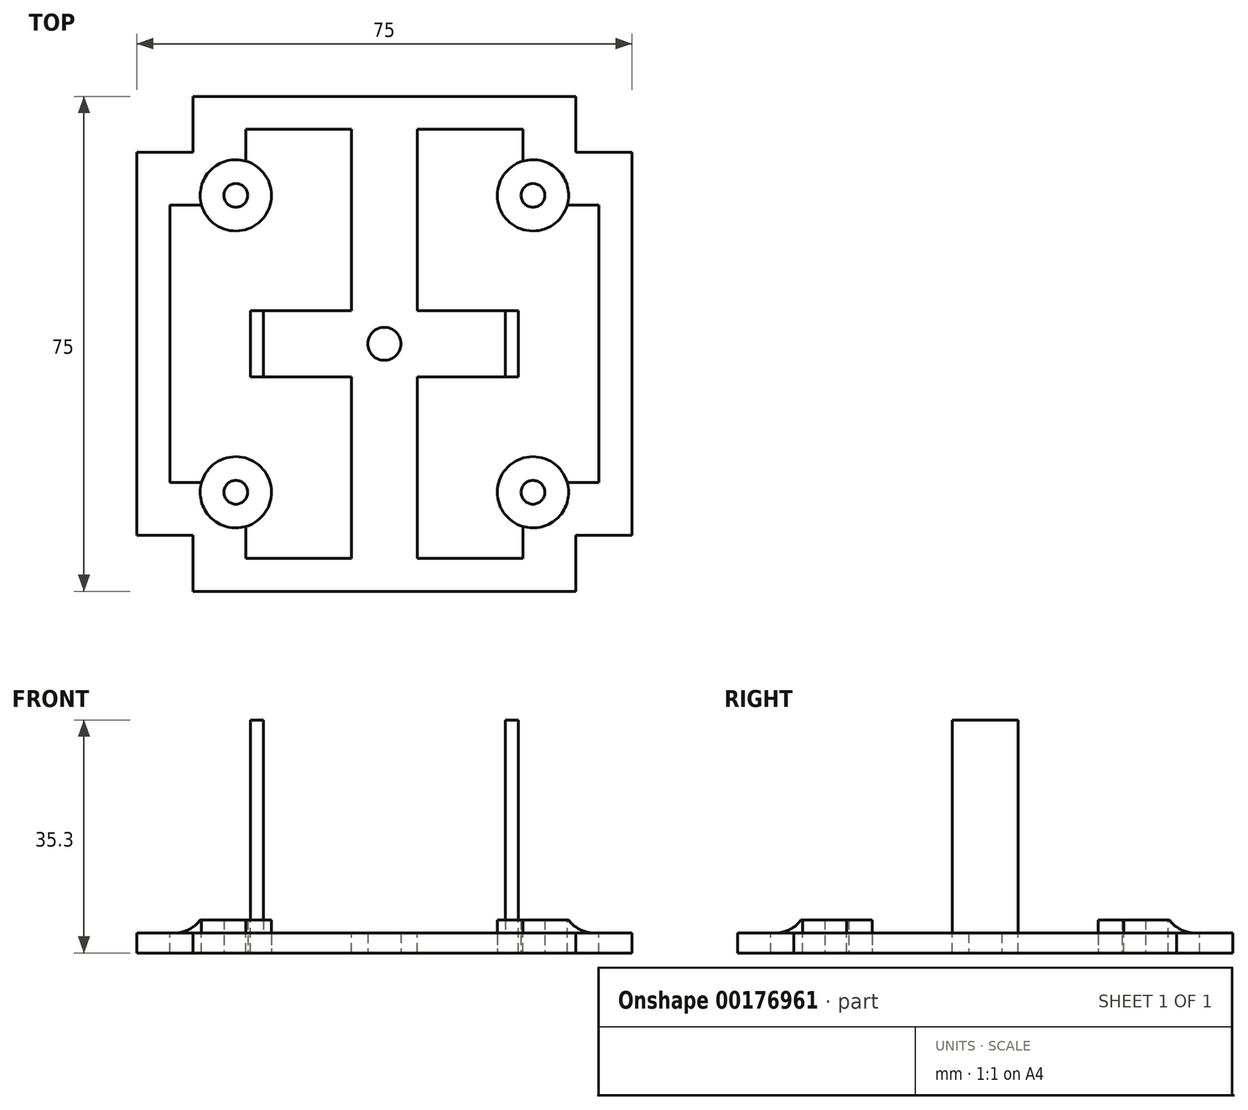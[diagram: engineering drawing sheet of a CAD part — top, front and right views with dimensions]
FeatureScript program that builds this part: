
annotation { "Feature Type Name" : "Feature", "Feature Type Description" : "" }
export const myFeature = defineFeature(function(context is Context, id is Id, definition is map)
    precondition{}
    {
        {
            assignVariable(context, id + "F0", {"name" : "thickness", "anyValue" : 3});
        }
        {
            var Q0;
            Q0=qCreatedBy(makeId("Top.planeOp"),FACE);
            var sketch = newSketch(context, id + "F1", { "sketchPlane" : qUnion([Q0])});
            skLineSegment(sketch, "E0.bottom", {"start": v(29, 37.5) * mm, "end": v(-29, 37.5) * mm});
            skLineSegment(sketch, "E0.top", {"start": v(29, -37.5) * mm, "end": v(-29, -37.5) * mm});
            skLineSegment(sketch, "E0.right", {"start": v(-37.5, 29) * mm, "end": v(-37.5, -29) * mm});
            skPoint(sketch, "E0.middle", {"position": v(0, 0) * mm});
            skLineSegment(sketch, "E1", {"start": v(-37.5, 29) * mm, "end": v(-29, 29) * mm});
            skLineSegment(sketch, "E2", {"start": v(-29, 29) * mm, "end": v(-29, 37.5) * mm});
            skLineSegment(sketch, "E3", {"start": v(0, 0) * mm, "end": v(0, 37.5) * mm, "construction": true});
            skLineSegment(sketch, "E4", {"start": v(0, 0) * mm, "end": v(50, 0) * mm, "construction": true});
            skLineSegment(sketch, "E5.MirrorCS", {"start": v(29, 29) * mm, "end": v(29, 37.5) * mm});
            skLineSegment(sketch, "E6.MirrorCS", {"start": v(37.5, 29) * mm, "end": v(29, 29) * mm});
            skLineSegment(sketch, "E7.MirrorCS", {"start": v(-37.5, -29) * mm, "end": v(-29, -29) * mm});
            skLineSegment(sketch, "E8.MirrorCS", {"start": v(-29, -29) * mm, "end": v(-29, -37.5) * mm});
            skLineSegment(sketch, "E9.MirrorCS", {"start": v(37.5, -29) * mm, "end": v(29, -29) * mm});
            skLineSegment(sketch, "E10.MirrorCS", {"start": v(37.5, -29) * mm, "end": v(37.5, 29) * mm});
            skLineSegment(sketch, "E11.MirrorCS", {"start": v(29, -29) * mm, "end": v(29, -37.5) * mm});
            skCircle(sketch, "E12", {"center": v(0, 0) * mm, "radius": 2.5 * mm});
            skSolve(sketch);
        }
        {
            var Q0;
            Q0=makeQuery(id+"F1.imprint","IMPRINT",FACE,{"disambiguationData":[TD([[makeQuery(id+"F1.imprint","IMPRINT",EDGE,{"derivedFrom":sQuery(id+"F1.wireOp",EDGE,"E0.bottom")}),1.0]])]});
            extrude(context, id + "F2", {"entities" : qUnion([Q0]), "depth" : (getVariable(context, 'thickness')) * mm});
        }
        {
            var Q0;
            Q0=makeQuery(id+"F2.opExtrude","CAP_FACE",FACE,{"disambiguationData":[OSD([sQuery(id+"F1.wireOp",EDGE,"E0.bottom"),sQuery(id+"F1.wireOp",EDGE,"E0.right"),sQuery(id+"F1.wireOp",EDGE,"E1"),sQuery(id+"F1.wireOp",EDGE,"E2"),sQuery(id+"F1.wireOp",EDGE,"E5.MirrorCS"),sQuery(id+"F1.wireOp",EDGE,"E6.MirrorCS"),sQuery(id+"F1.wireOp",EDGE,"E7.MirrorCS"),sQuery(id+"F1.wireOp",EDGE,"E8.MirrorCS"),sQuery(id+"F1.wireOp",EDGE,"E9.MirrorCS"),sQuery(id+"F1.wireOp",EDGE,"E10.MirrorCS"),sQuery(id+"F1.wireOp",EDGE,"E11.MirrorCS"),sQuery(id+"F1.wireOp",EDGE,"E0.top"),sQuery(id+"F1.wireOp",EDGE,"E12")])],"isStart":false});
            var sketch = newSketch(context, id + "F3", { "sketchPlane" : qUnion([Q0])});
            skPoint(sketch, "E13.middle", {"position": v(0, 0) * mm});
            skLineSegment(sketch, "E14.0", {"start": v(5, -32.5) * mm, "end": v(5, -5) * mm});
            skLineSegment(sketch, "E15.0", {"start": v(-5, -32.5) * mm, "end": v(-5, -5) * mm});
            skLineSegment(sketch, "E16", {"start": v(-17.9, -22.5) * mm, "end": v(17.9, -22.5) * mm, "construction": true});
            skLineSegment(sketch, "E17", {"start": v(-17.9, -22.5) * mm, "end": v(-17.9, 37.5) * mm, "construction": true});
            skLineSegment(sketch, "E18", {"start": v(17.9, -22.5) * mm, "end": v(17.9, 37.5) * mm, "construction": true});
            skLineSegment(sketch, "E19", {"start": v(-20.3, 5) * mm, "end": v(-5, 5) * mm});
            skLineSegment(sketch, "E20.MirrorCS", {"start": v(-20.3, -5) * mm, "end": v(-5, -5) * mm});
            skLineSegment(sketch, "E21.trimOffspring", {"start": v(-20.3, -5) * mm, "end": v(-20.3, 5) * mm});
            skLineSegment(sketch, "E22.MirrorCS", {"start": v(20.3, -5) * mm, "end": v(20.3, 5) * mm});
            skLineSegment(sketch, "E23.0", {"start": v(21, 32.5) * mm, "end": v(-21, 32.5) * mm});
            skLineSegment(sketch, "E24.0", {"start": v(-32.5, 21) * mm, "end": v(-32.5, -21) * mm});
            skLineSegment(sketch, "E25.0", {"start": v(-32.5, 21) * mm, "end": v(-21, 21) * mm});
            skLineSegment(sketch, "E26.0", {"start": v(-21, 21) * mm, "end": v(-21, 32.5) * mm});
            skLineSegment(sketch, "E27.MirrorCS", {"start": v(21, 21) * mm, "end": v(21, 32.5) * mm});
            skLineSegment(sketch, "E28.MirrorCS", {"start": v(32.5, 21) * mm, "end": v(21, 21) * mm});
            skLineSegment(sketch, "E29.MirrorCS", {"start": v(32.5, 21) * mm, "end": v(32.5, -21) * mm});
            skLineSegment(sketch, "E30.MirrorCS", {"start": v(32.5, -21) * mm, "end": v(21, -21) * mm});
            skLineSegment(sketch, "E31.MirrorCS", {"start": v(21, -21) * mm, "end": v(21, -32.5) * mm});
            skLineSegment(sketch, "E32.MirrorCS", {"start": v(21, -32.5) * mm, "end": v(-21, -32.5) * mm});
            skLineSegment(sketch, "E33.MirrorCS", {"start": v(-21, -21) * mm, "end": v(-21, -32.5) * mm});
            skLineSegment(sketch, "E34.MirrorCS", {"start": v(-32.5, -21) * mm, "end": v(-21, -21) * mm});
            skLineSegment(sketch, "E35.trimOffspring", {"start": v(-5, 5) * mm, "end": v(-5, 32.5) * mm});
            skLineSegment(sketch, "E36.trimOffspring", {"start": v(5, 5) * mm, "end": v(5, 32.5) * mm});
            skLineSegment(sketch, "E37.trimOffspring", {"start": v(5, 5) * mm, "end": v(20.3, 5) * mm});
            skLineSegment(sketch, "E38.trimOffspring", {"start": v(5, -5) * mm, "end": v(20.3, -5) * mm});
            skSolve(sketch);
        }
        {
            var Q0;
            {var subQ4=sQuery(id+"F3.wireOp",EDGE,"E15.0");Q0=makeQuery(id+"F3.imprint","IMPRINT",FACE,{"disambiguationData":[TD([[makeQuery(id+"F3.imprint","IMPRINT",EDGE,{"derivedFrom":subQ4}),1.0]])]});}
            var Q1;
            {var subQ5=sQuery(id+"F3.wireOp",EDGE,"E14.0");Q1=makeQuery(id+"F3.imprint","IMPRINT",FACE,{"disambiguationData":[TD([[makeQuery(id+"F3.imprint","IMPRINT",EDGE,{"derivedFrom":subQ5}),-1.0]])]});}
            extrude(context, id + "F4", {"entities" : qUnion([Q0, Q1]), "operationType" : NewBodyOperationType.REMOVE, "endBound" : BoundingType.THROUGH_ALL, "oppositeDirection" : true, "depth" : 25 * mm});
        }
        {
            var Q0;
            Q0=makeQuery(id+"F2.opExtrude","CAP_FACE",FACE,{"disambiguationData":[OSD([sQuery(id+"F1.wireOp",EDGE,"E0.bottom"),sQuery(id+"F1.wireOp",EDGE,"E0.right"),sQuery(id+"F1.wireOp",EDGE,"E1"),sQuery(id+"F1.wireOp",EDGE,"E2"),sQuery(id+"F1.wireOp",EDGE,"E5.MirrorCS"),sQuery(id+"F1.wireOp",EDGE,"E6.MirrorCS"),sQuery(id+"F1.wireOp",EDGE,"E7.MirrorCS"),sQuery(id+"F1.wireOp",EDGE,"E8.MirrorCS"),sQuery(id+"F1.wireOp",EDGE,"E9.MirrorCS"),sQuery(id+"F1.wireOp",EDGE,"E10.MirrorCS"),sQuery(id+"F1.wireOp",EDGE,"E11.MirrorCS"),sQuery(id+"F1.wireOp",EDGE,"E0.top"),sQuery(id+"F1.wireOp",EDGE,"E12")])],"isStart":false});
            var sketch = newSketch(context, id + "F5", { "sketchPlane" : qUnion([Q0])});
            skCircle(sketch, "E39", {"center": v(-22.5, 22.5) * mm, "radius": 1.8 * mm});
            skCircle(sketch, "E40", {"center": v(-22.5, 22.5) * mm, "radius": 5.4 * mm});
            skCircle(sketch, "E41.MirrorC", {"center": v(-22.5, -22.5) * mm, "radius": 1.8 * mm});
            skCircle(sketch, "E42.MirrorC", {"center": v(-22.5, -22.5) * mm, "radius": 5.4 * mm});
            skCircle(sketch, "E43.MirrorC", {"center": v(22.5, 22.5) * mm, "radius": 1.8 * mm});
            skCircle(sketch, "E44.MirrorC", {"center": v(22.5, 22.5) * mm, "radius": 5.4 * mm});
            skCircle(sketch, "E45.MirrorC", {"center": v(22.5, -22.5) * mm, "radius": 5.4 * mm});
            skCircle(sketch, "E46.MirrorC", {"center": v(22.5, -22.5) * mm, "radius": 1.8 * mm});
            skSolve(sketch);
        }
        {
            var Q0;
            Q0=qSketchRegion(id+"F5",true);
            extrude(context, id + "F6", {"entities" : qUnion([Q0]), "operationType" : NewBodyOperationType.ADD, "depth" : 2 * mm});
        }
        {
            var Q0;
            Q0=makeQuery(id+"F6.boolean.opBoolean","SPLIT",FACE,{"disambiguationData":[TD([makeQuery(id+"F6.opExtrude","SWEPT_FACE",FACE,{"disambiguationData":[OSD([sQuery(id+"F5.wireOp",EDGE,"E39")])]})])],"derivedFrom":makeQuery(id+"F2.opExtrude","CAP_FACE",FACE,{"disambiguationData":[OSD([sQuery(id+"F1.wireOp",EDGE,"E0.bottom"),sQuery(id+"F1.wireOp",EDGE,"E0.right"),sQuery(id+"F1.wireOp",EDGE,"E1"),sQuery(id+"F1.wireOp",EDGE,"E2"),sQuery(id+"F1.wireOp",EDGE,"E5.MirrorCS"),sQuery(id+"F1.wireOp",EDGE,"E6.MirrorCS"),sQuery(id+"F1.wireOp",EDGE,"E7.MirrorCS"),sQuery(id+"F1.wireOp",EDGE,"E8.MirrorCS"),sQuery(id+"F1.wireOp",EDGE,"E9.MirrorCS"),sQuery(id+"F1.wireOp",EDGE,"E10.MirrorCS"),sQuery(id+"F1.wireOp",EDGE,"E11.MirrorCS"),sQuery(id+"F1.wireOp",EDGE,"E0.top"),sQuery(id+"F1.wireOp",EDGE,"E12")])],"isStart":false})});
            var Q1;
            Q1=makeQuery(id+"F6.boolean.opBoolean","SPLIT",FACE,{"disambiguationData":[TD([makeQuery(id+"F6.opExtrude","SWEPT_FACE",FACE,{"disambiguationData":[OSD([sQuery(id+"F5.wireOp",EDGE,"E43.MirrorC")])]})])],"derivedFrom":makeQuery(id+"F2.opExtrude","CAP_FACE",FACE,{"disambiguationData":[OSD([sQuery(id+"F1.wireOp",EDGE,"E0.bottom"),sQuery(id+"F1.wireOp",EDGE,"E0.right"),sQuery(id+"F1.wireOp",EDGE,"E1"),sQuery(id+"F1.wireOp",EDGE,"E2"),sQuery(id+"F1.wireOp",EDGE,"E5.MirrorCS"),sQuery(id+"F1.wireOp",EDGE,"E6.MirrorCS"),sQuery(id+"F1.wireOp",EDGE,"E7.MirrorCS"),sQuery(id+"F1.wireOp",EDGE,"E8.MirrorCS"),sQuery(id+"F1.wireOp",EDGE,"E9.MirrorCS"),sQuery(id+"F1.wireOp",EDGE,"E10.MirrorCS"),sQuery(id+"F1.wireOp",EDGE,"E11.MirrorCS"),sQuery(id+"F1.wireOp",EDGE,"E0.top"),sQuery(id+"F1.wireOp",EDGE,"E12")])],"isStart":false})});
            var Q2;
            Q2=makeQuery(id+"F6.boolean.opBoolean","SPLIT",FACE,{"disambiguationData":[TD([makeQuery(id+"F6.opExtrude","SWEPT_FACE",FACE,{"disambiguationData":[OSD([sQuery(id+"F5.wireOp",EDGE,"E46.MirrorC")])]})])],"derivedFrom":makeQuery(id+"F2.opExtrude","CAP_FACE",FACE,{"disambiguationData":[OSD([sQuery(id+"F1.wireOp",EDGE,"E0.bottom"),sQuery(id+"F1.wireOp",EDGE,"E0.right"),sQuery(id+"F1.wireOp",EDGE,"E1"),sQuery(id+"F1.wireOp",EDGE,"E2"),sQuery(id+"F1.wireOp",EDGE,"E5.MirrorCS"),sQuery(id+"F1.wireOp",EDGE,"E6.MirrorCS"),sQuery(id+"F1.wireOp",EDGE,"E7.MirrorCS"),sQuery(id+"F1.wireOp",EDGE,"E8.MirrorCS"),sQuery(id+"F1.wireOp",EDGE,"E9.MirrorCS"),sQuery(id+"F1.wireOp",EDGE,"E10.MirrorCS"),sQuery(id+"F1.wireOp",EDGE,"E11.MirrorCS"),sQuery(id+"F1.wireOp",EDGE,"E0.top"),sQuery(id+"F1.wireOp",EDGE,"E12")])],"isStart":false})});
            var Q3;
            Q3=makeQuery(id+"F6.boolean.opBoolean","SPLIT",FACE,{"disambiguationData":[TD([makeQuery(id+"F6.opExtrude","SWEPT_FACE",FACE,{"disambiguationData":[OSD([sQuery(id+"F5.wireOp",EDGE,"E41.MirrorC")])]})])],"derivedFrom":makeQuery(id+"F2.opExtrude","CAP_FACE",FACE,{"disambiguationData":[OSD([sQuery(id+"F1.wireOp",EDGE,"E0.bottom"),sQuery(id+"F1.wireOp",EDGE,"E0.right"),sQuery(id+"F1.wireOp",EDGE,"E1"),sQuery(id+"F1.wireOp",EDGE,"E2"),sQuery(id+"F1.wireOp",EDGE,"E5.MirrorCS"),sQuery(id+"F1.wireOp",EDGE,"E6.MirrorCS"),sQuery(id+"F1.wireOp",EDGE,"E7.MirrorCS"),sQuery(id+"F1.wireOp",EDGE,"E8.MirrorCS"),sQuery(id+"F1.wireOp",EDGE,"E9.MirrorCS"),sQuery(id+"F1.wireOp",EDGE,"E10.MirrorCS"),sQuery(id+"F1.wireOp",EDGE,"E11.MirrorCS"),sQuery(id+"F1.wireOp",EDGE,"E0.top"),sQuery(id+"F1.wireOp",EDGE,"E12")])],"isStart":false})});
            extrude(context, id + "F7", {"entities" : qUnion([Q0, Q1, Q2, Q3]), "operationType" : NewBodyOperationType.REMOVE, "endBound" : BoundingType.THROUGH_ALL, "oppositeDirection" : true, "depth" : 25 * mm});
        }
        {
            var Q0;
            {var subQ0=sQuery(id+"F5.wireOp",EDGE,"E44.MirrorC");Q0=makeQuery(id+"F6.boolean.opBoolean","SPLIT",FACE,{"disambiguationData":[TD([makeQuery(id+"F4.boolean.opBoolean","COPY",FACE,{"derivedFrom":makeQuery(id+"F4.opExtrude","SWEPT_FACE",FACE,{"disambiguationData":[OSD([sQuery(id+"F3.wireOp",EDGE,"f52dab60-5a2c-4a32-b258-133c4f1d6454.trimOffspring")])]})})])],"derivedFrom":makeQuery(id+"F6.opExtrude","CAP_FACE",FACE,{"disambiguationData":[OSD([sQuery(id+"F5.wireOp",EDGE,"E43.MirrorC"),subQ0])],"isStart":true})});}
            var Q1;
            {var subQ0=sQuery(id+"F5.wireOp",EDGE,"E44.MirrorC");Q1=makeQuery(id+"F6.boolean.opBoolean","SPLIT",FACE,{"disambiguationData":[TD([makeQuery(id+"F4.boolean.opBoolean","COPY",FACE,{"derivedFrom":makeQuery(id+"F4.opExtrude","SWEPT_FACE",FACE,{"disambiguationData":[OSD([sQuery(id+"F3.wireOp",EDGE,"b3e9a3b4-25b0-4999-a88c-f1a30fad052b.trimOffspring")])]})})])],"derivedFrom":makeQuery(id+"F6.opExtrude","CAP_FACE",FACE,{"disambiguationData":[OSD([sQuery(id+"F5.wireOp",EDGE,"E43.MirrorC"),subQ0])],"isStart":true})});}
            var Q2;
            {var subQ0=sQuery(id+"F5.wireOp",EDGE,"E45.MirrorC");Q2=makeQuery(id+"F6.boolean.opBoolean","SPLIT",FACE,{"disambiguationData":[TD([makeQuery(id+"F4.boolean.opBoolean","COPY",FACE,{"derivedFrom":makeQuery(id+"F4.opExtrude","SWEPT_FACE",FACE,{"disambiguationData":[OSD([sQuery(id+"F3.wireOp",EDGE,"f979096a-dc96-4d13-bc05-f9a5557baaae0.MirrorCS")])]})})])],"derivedFrom":makeQuery(id+"F6.opExtrude","CAP_FACE",FACE,{"disambiguationData":[OSD([subQ0,sQuery(id+"F5.wireOp",EDGE,"E46.MirrorC")])],"isStart":true})});}
            var Q3;
            {var subQ0=sQuery(id+"F5.wireOp",EDGE,"E45.MirrorC");Q3=makeQuery(id+"F6.boolean.opBoolean","SPLIT",FACE,{"disambiguationData":[TD([makeQuery(id+"F4.boolean.opBoolean","COPY",FACE,{"derivedFrom":makeQuery(id+"F4.opExtrude","SWEPT_FACE",FACE,{"disambiguationData":[OSD([sQuery(id+"F3.wireOp",EDGE,"48047b57-8171-425c-94b1-7ed8ccb7c9670.MirrorCS")])]})})])],"derivedFrom":makeQuery(id+"F6.opExtrude","CAP_FACE",FACE,{"disambiguationData":[OSD([subQ0,sQuery(id+"F5.wireOp",EDGE,"E46.MirrorC")])],"isStart":true})});}
            var Q4;
            {var subQ0=sQuery(id+"F5.wireOp",EDGE,"E42.MirrorC");Q4=makeQuery(id+"F6.boolean.opBoolean","SPLIT",FACE,{"disambiguationData":[TD([makeQuery(id+"F4.boolean.opBoolean","COPY",FACE,{"derivedFrom":makeQuery(id+"F4.opExtrude","SWEPT_FACE",FACE,{"disambiguationData":[OSD([sQuery(id+"F3.wireOp",EDGE,"aedfb6cc-665d-4429-8bce-05d3141d4cb6.0")])]})})])],"derivedFrom":makeQuery(id+"F6.opExtrude","CAP_FACE",FACE,{"disambiguationData":[OSD([sQuery(id+"F5.wireOp",EDGE,"E41.MirrorC"),subQ0])],"isStart":true})});}
            var Q5;
            {var subQ0=sQuery(id+"F5.wireOp",EDGE,"E42.MirrorC");Q5=makeQuery(id+"F6.boolean.opBoolean","SPLIT",FACE,{"disambiguationData":[TD([makeQuery(id+"F4.boolean.opBoolean","COPY",FACE,{"derivedFrom":makeQuery(id+"F4.opExtrude","SWEPT_FACE",FACE,{"disambiguationData":[OSD([sQuery(id+"F3.wireOp",EDGE,"f759702b-d707-4b8b-8972-658867be496e.0")])]})})])],"derivedFrom":makeQuery(id+"F6.opExtrude","CAP_FACE",FACE,{"disambiguationData":[OSD([sQuery(id+"F5.wireOp",EDGE,"E41.MirrorC"),subQ0])],"isStart":true})});}
            var Q6;
            {var subQ0=sQuery(id+"F5.wireOp",EDGE,"E40");Q6=makeQuery(id+"F6.boolean.opBoolean","SPLIT",FACE,{"disambiguationData":[TD([makeQuery(id+"F4.boolean.opBoolean","COPY",FACE,{"derivedFrom":makeQuery(id+"F4.opExtrude","SWEPT_FACE",FACE,{"disambiguationData":[OSD([sQuery(id+"F3.wireOp",EDGE,"2a697884-57e0-4922-80c6-6aa455d0f8010.MirrorCS")])]})})])],"derivedFrom":makeQuery(id+"F6.opExtrude","CAP_FACE",FACE,{"disambiguationData":[OSD([sQuery(id+"F5.wireOp",EDGE,"E39"),subQ0])],"isStart":true})});}
            var Q7;
            {var subQ0=sQuery(id+"F5.wireOp",EDGE,"E40");Q7=makeQuery(id+"F6.boolean.opBoolean","SPLIT",FACE,{"disambiguationData":[TD([makeQuery(id+"F4.boolean.opBoolean","COPY",FACE,{"derivedFrom":makeQuery(id+"F4.opExtrude","SWEPT_FACE",FACE,{"disambiguationData":[OSD([sQuery(id+"F3.wireOp",EDGE,"10efca7f-4d4f-4726-b395-085f71b26c6a0.MirrorCS")])]})})])],"derivedFrom":makeQuery(id+"F6.opExtrude","CAP_FACE",FACE,{"disambiguationData":[OSD([sQuery(id+"F5.wireOp",EDGE,"E39"),subQ0])],"isStart":true})});}
            var Q8;
            Q8=makeQuery(id+"F2.opExtrude","CAP_FACE",FACE,{"disambiguationData":[OSD([sQuery(id+"F1.wireOp",EDGE,"E0.bottom"),sQuery(id+"F1.wireOp",EDGE,"E0.right"),sQuery(id+"F1.wireOp",EDGE,"E1"),sQuery(id+"F1.wireOp",EDGE,"E2"),sQuery(id+"F1.wireOp",EDGE,"E5.MirrorCS"),sQuery(id+"F1.wireOp",EDGE,"E6.MirrorCS"),sQuery(id+"F1.wireOp",EDGE,"E7.MirrorCS"),sQuery(id+"F1.wireOp",EDGE,"E8.MirrorCS"),sQuery(id+"F1.wireOp",EDGE,"E9.MirrorCS"),sQuery(id+"F1.wireOp",EDGE,"E10.MirrorCS"),sQuery(id+"F1.wireOp",EDGE,"E11.MirrorCS"),sQuery(id+"F1.wireOp",EDGE,"E0.top"),sQuery(id+"F1.wireOp",EDGE,"E12")])],"isStart":true});
            extrude(context, id + "F8", {"entities" : qUnion([Q0, Q1, Q2, Q3, Q4, Q5, Q6, Q7]), "operationType" : NewBodyOperationType.ADD, "endBound" : BoundingType.UP_TO_SURFACE, "endBoundEntityFace" : qUnion([Q8]), "depth" : 25 * mm});
        }
        {
            var Q0;
            {var subQ3=sQuery(id+"F1.wireOp",EDGE,"E1");var subQ5=sQuery(id+"F1.wireOp",EDGE,"E9.MirrorCS");var subQ7=sQuery(id+"F1.wireOp",EDGE,"E12");var subQ9=sQuery(id+"F1.wireOp",EDGE,"E0.top");var subQ10=sQuery(id+"F1.wireOp",EDGE,"E10.MirrorCS");var subQ11=sQuery(id+"F1.wireOp",EDGE,"E11.MirrorCS");var subQ13=sQuery(id+"F1.wireOp",EDGE,"E2");var subQ17=sQuery(id+"F1.wireOp",EDGE,"E0.right");var subQ19=sQuery(id+"F1.wireOp",EDGE,"E0.bottom");var subQ20=sQuery(id+"F1.wireOp",EDGE,"E5.MirrorCS");var subQ22=sQuery(id+"F1.wireOp",EDGE,"E6.MirrorCS");var subQ23=sQuery(id+"F1.wireOp",EDGE,"E7.MirrorCS");var subQ25=sQuery(id+"F1.wireOp",EDGE,"E8.MirrorCS");Q0=makeQuery(id+"F6.boolean.opBoolean","SPLIT",FACE,{"disambiguationData":[TD([makeQuery(id+"F2.opExtrude","SWEPT_FACE",FACE,{"disambiguationData":[OSD([subQ19])]})])],"derivedFrom":makeQuery(id+"F2.opExtrude","CAP_FACE",FACE,{"disambiguationData":[OSD([subQ19,subQ17,subQ3,subQ13,subQ20,subQ22,subQ23,subQ25,subQ5,subQ10,subQ11,subQ9,subQ7])],"isStart":false})});}
            var sketch = newSketch(context, id + "F9", { "sketchPlane" : qUnion([Q0])});
            skLineSegment(sketch, "E47.bottom", {"start": v(-20.3, 5) * mm, "end": v(-18.3, 5) * mm});
            skLineSegment(sketch, "E47.top", {"start": v(-20.3, -5) * mm, "end": v(-18.3, -5) * mm});
            skLineSegment(sketch, "E47.left", {"start": v(-20.3, 5) * mm, "end": v(-20.3, -5) * mm});
            skLineSegment(sketch, "E47.right", {"start": v(-18.3, 5) * mm, "end": v(-18.3, -5) * mm});
            skLineSegment(sketch, "E48.MirrorCS", {"start": v(20.3, 5) * mm, "end": v(18.3, 5) * mm});
            skLineSegment(sketch, "E49.MirrorCS", {"start": v(20.3, -5) * mm, "end": v(18.3, -5) * mm});
            skLineSegment(sketch, "E50.MirrorCS", {"start": v(20.3, 5) * mm, "end": v(20.3, -5) * mm});
            skLineSegment(sketch, "E51.MirrorCS", {"start": v(18.3, 5) * mm, "end": v(18.3, -5) * mm});
            skSolve(sketch);
        }
        {
            var Q0;
            Q0=makeQuery(id+"F9.imprint","IMPRINT",FACE,{"disambiguationData":[TD([[makeQuery(id+"F9.imprint","IMPRINT",EDGE,{"derivedFrom":sQuery(id+"F9.wireOp",EDGE,"E47.bottom")}),-1.0]])]});
            var Q1;
            Q1=makeQuery(id+"F9.imprint","IMPRINT",FACE,{"disambiguationData":[TD([[makeQuery(id+"F9.imprint","IMPRINT",EDGE,{"derivedFrom":sQuery(id+"F9.wireOp",EDGE,"E48.MirrorCS")}),-1.0]])]});
            extrude(context, id + "F10", {"entities" : qUnion([Q0, Q1]), "operationType" : NewBodyOperationType.ADD, "depth" : 32.3 * mm});
        }
        {
            var Q0;
            Q0=makeQuery(id+"F6.boolean.opBoolean","SPLIT",EDGE,{"disambiguationData":[OD(1.0)],"derivedFrom":makeQuery(id+"F6.opExtrude","CAP_EDGE",EDGE,{"disambiguationData":[OSD([sQuery(id+"F5.wireOp",EDGE,"E44.MirrorC")])],"isStart":true})});
            var Q1;
            Q1=makeQuery(id+"F6.boolean.opBoolean","SPLIT",EDGE,{"disambiguationData":[OD(1.0)],"derivedFrom":makeQuery(id+"F6.opExtrude","CAP_EDGE",EDGE,{"disambiguationData":[OSD([sQuery(id+"F5.wireOp",EDGE,"E40")])],"isStart":true})});
            var Q2;
            Q2=makeQuery(id+"F6.boolean.opBoolean","SPLIT",EDGE,{"disambiguationData":[OD(1.0)],"derivedFrom":makeQuery(id+"F6.opExtrude","CAP_EDGE",EDGE,{"disambiguationData":[OSD([sQuery(id+"F5.wireOp",EDGE,"E42.MirrorC")])],"isStart":true})});
            var Q3;
            Q3=makeQuery(id+"F6.boolean.opBoolean","SPLIT",EDGE,{"disambiguationData":[OD(1.0)],"derivedFrom":makeQuery(id+"F6.opExtrude","CAP_EDGE",EDGE,{"disambiguationData":[OSD([sQuery(id+"F5.wireOp",EDGE,"E45.MirrorC")])],"isStart":true})});
            fillet(context, id + "F11", {"entities" : qUnion([Q0, Q1, Q2, Q3]), "radius" : 5 * mm, "tangentPropagation" : true, "allowEdgeOverflow" : false});
        }
    });
